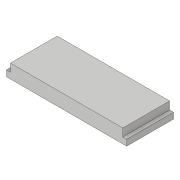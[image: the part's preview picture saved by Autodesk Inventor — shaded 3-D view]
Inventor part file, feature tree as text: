
AUTODESK INVENTOR PART (.ipt)
format: ipt  version: 2018.3 (Build 223284000, 284)  size: 89,088 bytes
history: native  units: in
note: dims shown in document units (in); Inventor stores cm internally (conversion verified against a paired STEP export)
features: extrude x2, sketch x2
ambient origin geometry x8: Origin, YZ Plane, XZ Plane, XY Plane, X Axis, Y Axis, Z Axis, Center Point
bodies: Solid1 (feature_tree)
feature tree (4):
  extrude  "Extrusion1"  Depth=0.75in
  extrude  "Extrusion5"  Depth=0.0625in
  sketch  "Sketch1"  dims[d0=1.925in d1=0.75in]
  sketch  "Sketch5"  dims[d2=0.221in d3=0.0in d17=0.0625in d18=0.0625in d19=0.125in d20=0.0in]
